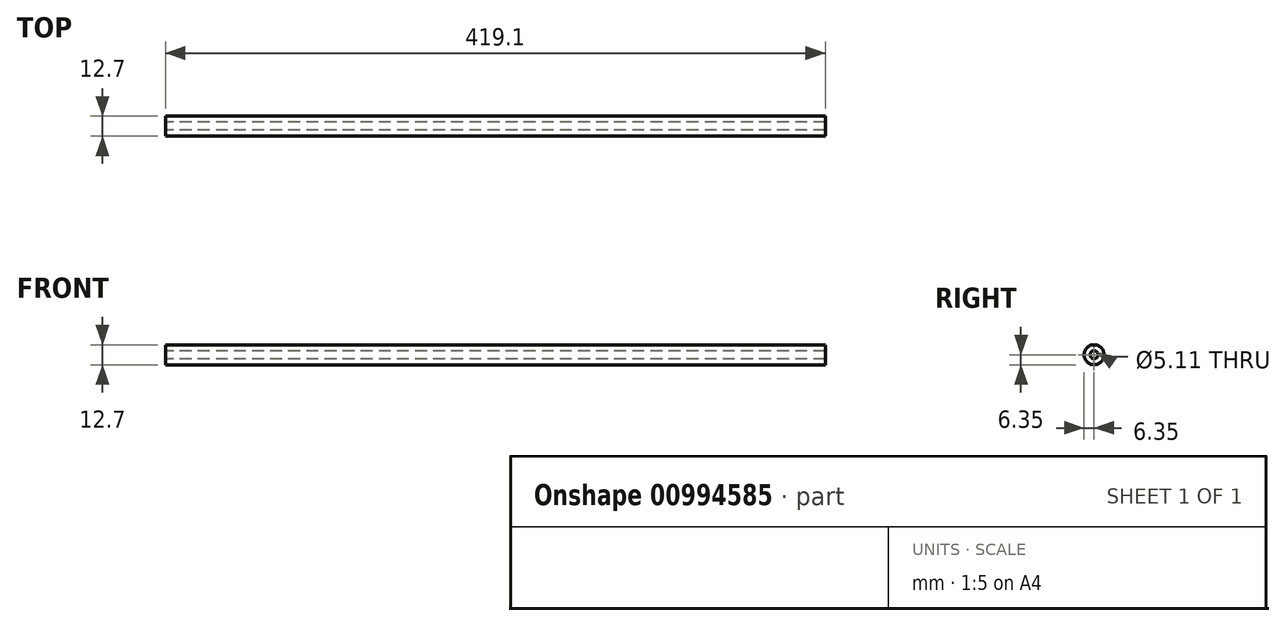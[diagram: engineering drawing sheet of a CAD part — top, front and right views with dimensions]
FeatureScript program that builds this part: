
annotation { "Feature Type Name" : "Feature", "Feature Type Description" : "" }
export const myFeature = defineFeature(function(context is Context, id is Id, definition is map)
    precondition{}
    {
        {
            var Q0;
            Q0=qCreatedBy(makeId("Right.planeOp"),FACE);
            var sketch = newSketch(context, id + "F0", { "sketchPlane" : qUnion([Q0])});
            skCircle(sketch, "E0", {"center": v(0, 0) * mm, "radius": 6.35 * mm});
            skSolve(sketch);
        }
        {
            var Q0;
            Q0=makeQuery(id+"F0.imprint","IMPRINT",FACE,{"disambiguationData":[TD([[makeQuery(id+"F0.imprint","IMPRINT",EDGE,{"derivedFrom":sQuery(id+"F0.wireOp",EDGE,"E0")}),1.0]])]});
            extrude(context, id + "F1", {"entities" : qUnion([Q0]), "depth" : 419.1 * mm, "offsetDistance" : 25.4 * mm});
        }
        {
            var Q0;
            Q0=makeQuery(id+"F1.opExtrude","CAP_FACE",FACE,{"disambiguationData":[OSD([sQuery(id+"F0.wireOp",EDGE,"E0"),sQuery(id+"F0.wireOp",EDGE,"diy2eWKF-TECT-u0jW-z3iu-OB6Dt8JxrE2p")])],"isStart":true});
            var sketch = newSketch(context, id + "F2", { "sketchPlane" : qUnion([Q0])});
            skPoint(sketch, "E1", {"position": v(0, 0) * mm});
            skSolve(sketch);
        }
        {
            var Q0;
            Q0=sQuery(id+"F2.wireOp",VERTEX,"E1");
            var Q1;
            Q1=makeQuery(id+"F1.opExtrude","SWEPT_BODY",BODY,{"disambiguationData":[OSD([sQuery(id+"F0.wireOp",EDGE,"E0"),sQuery(id+"F0.wireOp",EDGE,"diy2eWKF-TECT-u0jW-z3iu-OB6Dt8JxrE2p")])]});
            hole(context, id + "F3", {"style" : HoleStyle.SIMPLE, "endStyle" : HoleEndStyle.THROUGH, "standardTappedOrClearance" : lookupTablePath({ "standard" : "ANSI", "engagement" : "75%", "pitch" : "20 tpi", "size" : "1/4", "type" : "Tapped" }), "standardBlindInLast" : lookupTablePath({ "standard" : "ANSI", "fit" : "Normal", "engagement" : "75%", "pitch" : "20 tpi", "size" : "1/4", "type" : "Clearance & tapped" }), "holeDiameter" : 5.1 * mm, "majorDiameter" : 6.35 * mm, "showTappedDepth" : true, "isTappedThrough" : true, "tappedDepth" : 19.05 * mm, "tapClearance" : 3, "locations" : qUnion([Q0]), "scope" : qUnion([Q1])});
        }
    });
